# Revit family: Dryer_Weight-Rated_Milnor_M170-Electric
name_source: partatom
category: Mechanical Equipment
units: mm (PartAtom-declared; Revit-internal decimal feet)

## family parameters
Always vertical = No
Classification Number = 23.45.70.11.14.17
Cut with Voids When Loaded = No
Maintain Annotation Orientation = No
Part Type = Normal
Room Calculation Point = No
Round Connector Dimension = Use Radius
Shared = No
Work Plane-Based = Yes

## types (6) — shared parameters
Assembly Code = E1010610
Capacity = 170 lbs Dry Weight
Compressed Air Connection Diameter = 0' - 0 1/4"
Cylinder Depth = 3' - 6 1/2"
Cylinder Diameter = 4' - 3 1/2"
Cylinder Volume = 51.2 CF
Default Elevation = 0' - 0"
Description = Milnor Commercial Laundry Dryer - Electric Model M170 as Specified
Door Base from FF = 2' - 9 3/8"
Door Opening = 2' - 7 3/8"
Door Opening Depth = 3' - 1 7/8"
Door Thickness = 0' - 1"
Electrical CL from FF = 6' - 5 1/2"
Electrical CL from Side = 0' - 2 1/8"
Exhaust CL from FF = 1' - 7 1/4"
Exhaust CL from Side = 1' - 2"
Exhaust Diameter = 1' - 6"
FSS Water Connection CL from FF = 6' - 8 7/8"
FSS Water Connection Diameter = 0' - 0 3/4"
FSS Water Connection from Side = 0' - 2 1/4"
Heat Input = 429900.0 Btu/h
Keynote = 11110
Manufacturer = Pellerin Milnor Corp
Manufacturer Fax = 504-468-3094
Manufacturer Website = http://www.milnor.com
Model = M170
Number of Poles = 1
Phase = 3
Product Data = http://www.arcat.com
Reversing = Yes
Revision = R1_04-2011
Sales Information = http://www.milnor.com
Send Message = http://www.arcat.com
URL = http://www.milnor.com
Unit Depth = 5' - 2 1/2"
Unit Height = 8' - 7 15/16"
Unit Weight = 2103
Unit Width = 4' - 7 1/2"
exhaustrad = 0' - 9"
fsswaterrad = 0' - 0 3/8"
gasrad = 0' - 0 1/4"
zero-valued in all types: Expected Lifespan (Years), Maintenance Schedule (Months), Warranty Duration (Years)

## per-type parameters (varying)
| type | Air Flow | Circuit Breaker Size | Frequency | MEP Amperage | Number of Wires | Oven kW Size | Voltage_MEP |
| 416-50-3ph 250A CB | 4400 CFM | 250 A | 50 Hz | 191 A | 4 | 105000 W | 416 V |
| 380-50-3ph 250A CB | 4400 CFM | 250 A | 50 Hz | 176 A | 4 | 105000 W | 380 V |
| 575-60-3ph 150A CB | 3770 CFM | 150 A | 60 Hz | 165 A | 3 | 90000 W | 575 V |
| 480-60-3ph 225A CB | 3770 CFM | 225 A | 60 Hz | 166 A | 3 | 126000 W | 480 V |
| 460-60-3ph 200A CB | 3770 CFM | 200 A | 60 Hz | 159 A | 3 | 115000 W | 460 V |
| 440-60-3ph 200A CB | 3770 CFM | 200 A | 60 Hz | 152 A | 3 | 105000 W | 440 V |

## geometry (parser evidence)
native form markers: Sweep x2
no freeform markers — native parametric forms only
